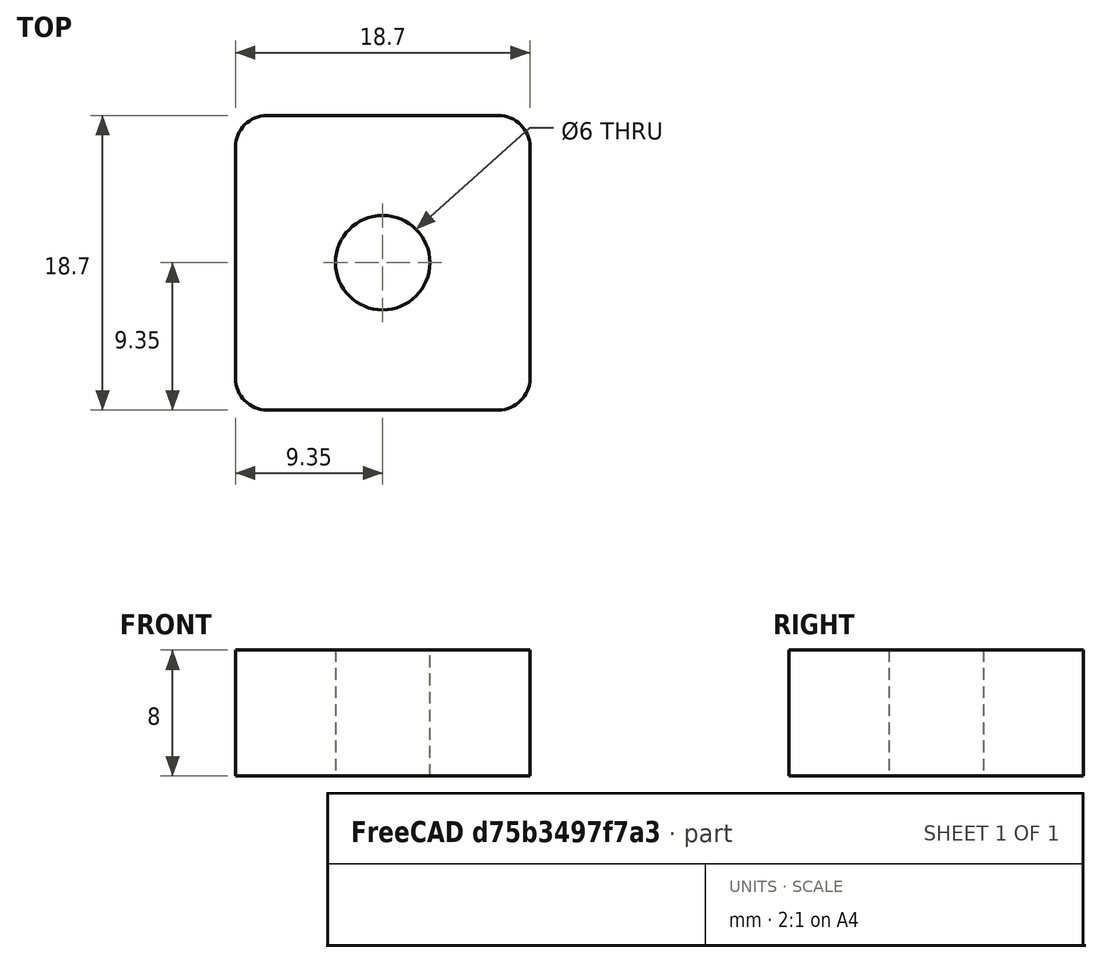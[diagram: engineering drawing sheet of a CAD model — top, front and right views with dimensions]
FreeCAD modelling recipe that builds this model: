
FCSTD DOCUMENT  (FreeCAD 0.19R24366 (Git))
Label: Flexible coolant pipe mount for LEDs spacer 8mm
License: All rights reserved
LicenseURL: http://en.wikipedia.org/wiki/All_rights_reserved
objects: Sketcher::SketchObject×1, PartDesign::Pad×1, PartDesign::Body×1
note: 4 computed .brp shape members not serialized (recipe doc carries the construction recipe); baked Part::Feature solids carry a one-line shape summary decoded from their .brp

FEATURE [Sketcher::SketchObject] Sketch
  FullyConstrained = true
  MapMode = 5
  Support = -> [XY_Plane]
  sketch-geometry (9):
    g0: Circle CenterX=0 CenterY=0 CenterZ=0 NormalX=0 NormalY=0 NormalZ=1 AngleXU=0 Radius=3
    g1: LineSegment StartX=-7.35 StartY=9.35 StartZ=0 EndX=7.35 EndY=9.35 EndZ=0
    g2: LineSegment StartX=9.35 StartY=7.35 StartZ=0 EndX=9.35 EndY=-7.35 EndZ=0
    g3: LineSegment StartX=7.35 StartY=-9.35 StartZ=0 EndX=-7.35 EndY=-9.35 EndZ=0
    g4: LineSegment StartX=-9.35 StartY=-7.35 StartZ=0 EndX=-9.35 EndY=7.35 EndZ=0
    g5: ArcOfCircle CenterX=-7.35 CenterY=7.35 CenterZ=0 NormalX=0 NormalY=0 NormalZ=1 AngleXU=0 Radius=2 StartAngle=1.5708 EndAngle=3.14159
    g6: ArcOfCircle CenterX=-7.35 CenterY=-7.35 CenterZ=0 NormalX=0 NormalY=0 NormalZ=1 AngleXU=0 Radius=2 StartAngle=3.14159 EndAngle=4.71239
    g7: ArcOfCircle CenterX=7.35 CenterY=-7.35 CenterZ=0 NormalX=0 NormalY=0 NormalZ=1 AngleXU=0 Radius=2 StartAngle=4.71239 EndAngle=6.28319
    g8: ArcOfCircle CenterX=7.35 CenterY=7.35 CenterZ=0 NormalX=0 NormalY=0 NormalZ=1 AngleXU=0 Radius=2 StartAngle=0 EndAngle=1.5708
  constraints (20):
    c: Coincident(g0,g-1)
    c: Horizontal(g1)
    c: Vertical(g2)
    c: Equal(g4,g1)
    c: Tangent(g1,g5) = 1.5708
    c: Tangent(g4,g5) = 1.5708
    c: Tangent(g4,g6) = 1.5708
    c: Tangent(g3,g6) = 1.5708
    c: Tangent(g2,g7) = 1.5708
    c: Tangent(g3,g7) = 1.5708
    c: Tangent(g1,g8) = 1.5708
    c: Tangent(g2,g8) = 1.5708
    c: Equal(g5,g6)
    c: Equal(g6,g7)
    c: Equal(g7,g8)
    c: Radius(g5) = 2
    c: Symmetric(g4,g4,g-1)
    c: Symmetric(g3,g3,g-2)
    c: DistanceY(g3,g1) = 18.7
    c: Radius(g0) = 3
FEATURE [PartDesign::Pad] Pad
  Direction = (1,1,1)
  Length = 8
  Length2 = 100
  Profile = -> Sketch
  Type = 0
FEATURE [PartDesign::Body] Body
  Group = -> [Sketch,Pad]
  Origin = -> Origin
  Tip = -> Pad
